FCSTD DOCUMENT  (FreeCAD 0.18R16110 (Git))
Label: 8sidePnew
License: All rights reserved
LicenseURL: http://en.wikipedia.org/wiki/All_rights_reserved
objects: Sketcher::SketchObject×1
note: 1 computed .brp shape members not serialized (recipe doc carries the construction recipe); baked Part::Feature solids carry a one-line shape summary decoded from their .brp

FEATURE [Sketcher::SketchObject] Sketch
  sketch-geometry (30):
    g0: LineSegment [constr] StartX=-929.209 StartY=-82.7087 StartZ=0 EndX=-598.566 EndY=-715.534 EndZ=0
    g1: LineSegment [constr] StartX=-598.566 StartY=-715.534 StartZ=0 EndX=82.7087 EndY=-929.209 EndZ=0
    g2: LineSegment [constr] StartX=82.7087 StartY=-929.209 StartZ=0 EndX=715.534 EndY=-598.566 EndZ=0
    g3: LineSegment [constr] StartX=715.534 StartY=-598.566 StartZ=0 EndX=929.209 EndY=82.7087 EndZ=0
    g4: LineSegment [constr] StartX=929.209 StartY=82.7087 StartZ=0 EndX=598.566 EndY=715.534 EndZ=0
    g5: LineSegment [constr] StartX=598.566 StartY=715.534 StartZ=0 EndX=-82.7087 EndY=929.209 EndZ=0
    g6: LineSegment [constr] StartX=-82.7087 StartY=929.209 StartZ=0 EndX=-715.534 EndY=598.566 EndZ=0
    g7: LineSegment [constr] StartX=-715.534 StartY=598.566 StartZ=0 EndX=-929.209 EndY=-82.7087 EndZ=0
    g8: Circle [constr] CenterX=0 CenterY=0 CenterZ=0 NormalX=0 NormalY=0 NormalZ=1 AngleXU=0 Radius=932.883
    g9: LineSegment [constr] StartX=-488.009 StartY=-67.0103 StartZ=0 EndX=-297.691 EndY=-392.458 EndZ=0
    g10: LineSegment [constr] StartX=-297.691 StartY=-392.458 StartZ=0 EndX=67.0103 EndY=-488.009 EndZ=0
    g11: LineSegment [constr] StartX=67.0103 StartY=-488.009 StartZ=0 EndX=392.458 EndY=-297.691 EndZ=0
    g12: LineSegment [constr] StartX=392.458 StartY=-297.691 StartZ=0 EndX=488.009 EndY=67.0103 EndZ=0
    g13: LineSegment [constr] StartX=488.009 StartY=67.0103 StartZ=0 EndX=297.691 EndY=392.458 EndZ=0
    g14: LineSegment [constr] StartX=297.691 StartY=392.458 StartZ=0 EndX=-67.0103 EndY=488.009 EndZ=0
    g15: LineSegment [constr] StartX=-67.0103 StartY=488.009 StartZ=0 EndX=-392.458 EndY=297.691 EndZ=0
    g16: LineSegment [constr] StartX=-392.458 StartY=297.691 StartZ=0 EndX=-488.009 EndY=-67.0103 EndZ=0
    g17: Circle [constr] CenterX=0 CenterY=0 CenterZ=0 NormalX=0 NormalY=0 NormalZ=1 AngleXU=0 Radius=492.588
    g18: LineSegment [constr] StartX=-715.534 StartY=598.566 StartZ=0 EndX=-67.0103 EndY=488.009 EndZ=0
    g19: LineSegment [constr] StartX=-82.7087 StartY=929.209 StartZ=0 EndX=297.691 EndY=392.458 EndZ=0
    g20: LineSegment [constr] StartX=598.566 StartY=715.534 StartZ=0 EndX=488.009 EndY=67.0103 EndZ=0
    g21: LineSegment [constr] StartX=929.209 StartY=82.7087 StartZ=0 EndX=392.458 EndY=-297.691 EndZ=0
    g22: LineSegment [constr] StartX=715.534 StartY=-598.566 StartZ=0 EndX=67.0103 EndY=-488.009 EndZ=0
    g23: LineSegment [constr] StartX=82.7087 StartY=-929.209 StartZ=0 EndX=-297.691 EndY=-392.458 EndZ=0
    g24: LineSegment [constr] StartX=-598.566 StartY=-715.534 StartZ=0 EndX=-488.009 EndY=-67.0103 EndZ=0
    g25: LineSegment [constr] StartX=-929.209 StartY=-82.7087 StartZ=0 EndX=-392.458 EndY=297.691 EndZ=0
    g26: LineSegment StartX=-606 StartY=606 StartZ=0 EndX=-606 EndY=-606 EndZ=0
    g27: LineSegment StartX=-606 StartY=-606 StartZ=0 EndX=606 EndY=-606 EndZ=0
    g28: LineSegment StartX=606 StartY=-606 StartZ=0 EndX=606 EndY=606 EndZ=0
    g29: LineSegment StartX=606 StartY=606 StartZ=0 EndX=-606 EndY=606 EndZ=0
  constraints (61):
    c: Coincident(g0,g1)
    c: Coincident(g1,g2)
    c: Coincident(g2,g3)
    c: Coincident(g3,g4)
    c: Coincident(g4,g5)
    c: Coincident(g5,g6)
    c: Equal(g0, g1-g7) x7
    c: PointOnObject(g0,g8)
    c: PointOnObject(g1,g8)
    c: PointOnObject(g2,g8)
    c: PointOnObject(g3,g8)
    c: PointOnObject(g4,g8)
    c: PointOnObject(g5,g8)
    c: PointOnObject(g6,g8)
    c: Coincident(g8,g-1)
    c: Coincident(g9,g10)
    c: Coincident(g10,g11)
    c: Coincident(g11,g12)
    c: Coincident(g12,g13)
    c: Coincident(g13,g14)
    c: Coincident(g14,g15)
    c: Coincident(g15,g16)
    c: Coincident(g16,g9)
    c: Equal(g9, g10-g16) x7
    c: PointOnObject(g9,g17)
    c: PointOnObject(g10,g17)
    c: PointOnObject(g11,g17)
    c: PointOnObject(g12,g17)
    c: PointOnObject(g13,g17)
    c: PointOnObject(g14,g17)
    c: PointOnObject(g15,g17)
    c: PointOnObject(g16,g17)
    c: Coincident(g17,g-1)
    c: Coincident(g18,g6)
    c: Coincident(g18,g14)
    c: Coincident(g19,g5)
    c: Coincident(g19,g13)
    c: Coincident(g20,g4)
    c: Coincident(g20,g12)
    c: Coincident(g21,g3)
    c: Coincident(g21,g11)
    c: Coincident(g22,g2)
    c: Coincident(g22,g10)
    c: Coincident(g23,g1)
    c: Coincident(g24,g0)
    c: Coincident(g24,g9)
    c: Coincident(g25,g0)
    c: Coincident(g0,g7)
    c: Coincident(g6,g7)
    c: PointOnObject(g0,g8)
    c: Coincident(g26,g27)
    c: Coincident(g27,g28)
    c: Coincident(g28,g29)
    c: Coincident(g29,g26)
    c: Equal(g26,g27)
    c: Equal(g26,g28)
    c: Equal(g26,g29)
    c: Distance(g28) = 1212
    c: Horizontal(g29)
    c: Coincident(g23,g9)
    c: Coincident(g25,g15)
